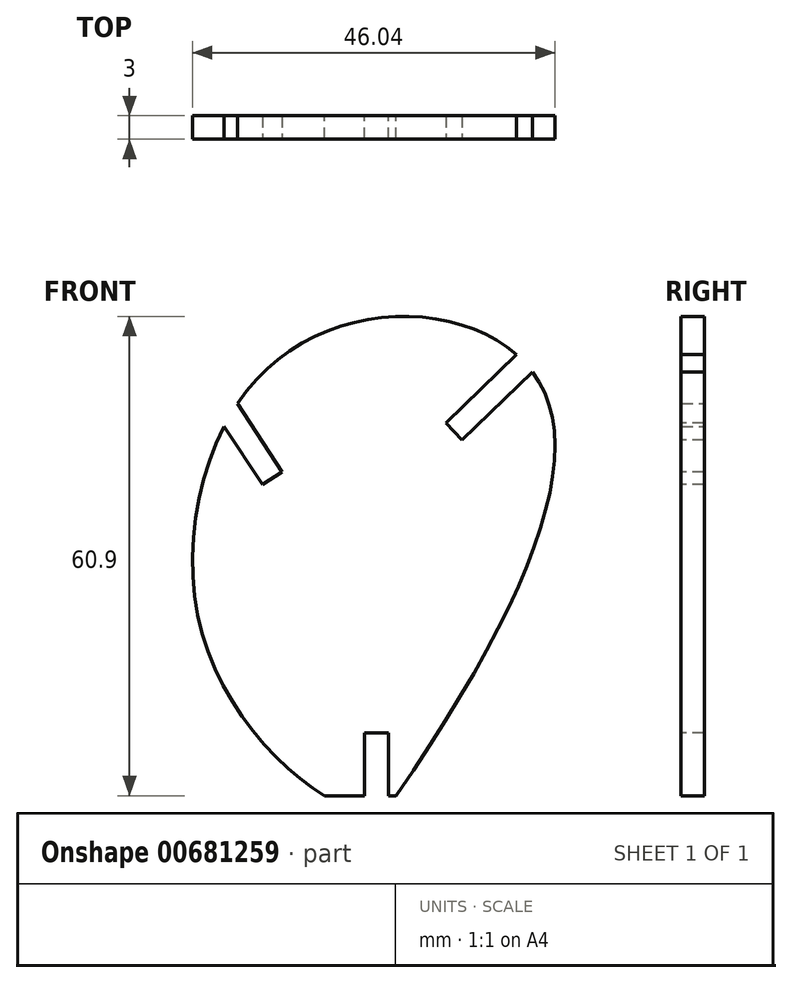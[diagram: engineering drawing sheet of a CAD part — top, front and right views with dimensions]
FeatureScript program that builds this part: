
annotation { "Feature Type Name" : "Feature", "Feature Type Description" : "" }
export const myFeature = defineFeature(function(context is Context, id is Id, definition is map)
    precondition{}
    {
        {
            assignVariable(context, id + "F0", {"name" : "MaterialDepth", "anyValue" : 3 * mm});
        }
        {
            var Q0;
            Q0=qCreatedBy(makeId("Front.planeOp"),FACE);
            var sketch = newSketch(context, id + "F1", { "sketchPlane" : qUnion([Q0])});
            skLineSegment(sketch, "E0", {"start": v(0, 53.6) * mm, "end": v(0, -7.3) * mm, "construction": true});
            skFitSpline(sketch, "E1", {"points": [v(-6.58, 0) * mm, v(-22.5, 22) * mm, v(-15.2, 52.94) * mm, v(6.9, 60.67) * mm, v(21.7, 50.29) * mm, v(2.48, 0) * mm], "startDerivative": vector(-102.35, 61.83) * mm, "endDerivative": vector(-172.56, -250.25) * mm});
            skLineSegment(sketch, "E2", {"start": v(-6.58, 0) * mm, "end": v(2.48, 0) * mm});
            skSolve(sketch);
        }
        {
            var Q0;
            Q0=makeQuery(id+"F1.imprint","IMPRINT",FACE,{"disambiguationData":[TD([[makeQuery(id+"F1.imprint","IMPRINT",EDGE,{"derivedFrom":sQuery(id+"F1.wireOp",EDGE,"E1")}),-1.0]])]});
            extrude(context, id + "F2", {"entities" : qUnion([Q0]), "endBound" : BoundingType.SYMMETRIC, "depth" : getVariable(context, 'MaterialDepth'), "offsetDistance" : 25 * mm});
        }
        {
            var Q0;
            Q0=makeQuery(id+"F2.opExtrude","CAP_FACE",FACE,{"disambiguationData":[OSD([sQuery(id+"F1.wireOp",EDGE,"E1"),sQuery(id+"F1.wireOp",EDGE,"E2")])],"isStart":false});
            var sketch = newSketch(context, id + "F3", { "sketchPlane" : qUnion([Q0])});
            skPoint(sketch, "E3", {"position": v(-18.52, 48.4) * mm});
            skLineSegment(sketch, "E4", {"start": v(-18.52, 48.4) * mm, "end": v(-14.84, 42.77) * mm, "construction": true});
            skLineSegment(sketch, "E5", {"start": v(-23.38, 45.24) * mm, "end": v(-18.52, 48.4) * mm, "construction": true});
            skLineSegment(sketch, "E6", {"start": v(-25.05, 55.66) * mm, "end": v(-23.8, 56.48) * mm});
            skLineSegment(sketch, "E7.MirrorCS", {"start": v(-14.51, 39.52) * mm, "end": v(-13.26, 40.34) * mm});
            skLineSegment(sketch, "E8", {"start": v(-25.05, 55.66) * mm, "end": v(-14.51, 39.52) * mm});
            skLineSegment(sketch, "E9.MirrorCS", {"start": v(-22.54, 57.3) * mm, "end": v(-23.8, 56.48) * mm});
            skLineSegment(sketch, "E10.MirrorCS", {"start": v(-22.54, 57.3) * mm, "end": v(-12, 41.16) * mm});
            skLineSegment(sketch, "E11.MirrorCS", {"start": v(-12, 41.16) * mm, "end": v(-13.26, 40.34) * mm});
            skPoint(sketch, "E12", {"position": v(18.83, 55) * mm});
            skLineSegment(sketch, "E13", {"start": v(18.83, 55) * mm, "end": v(12.2, 48.6) * mm, "construction": true});
            skLineSegment(sketch, "E14", {"start": v(18.83, 55) * mm, "end": v(19.82, 53.97) * mm, "construction": true});
            skLineSegment(sketch, "E15", {"start": v(10.88, 45.22) * mm, "end": v(9.84, 46.3) * mm});
            skLineSegment(sketch, "E16.MirrorCS", {"start": v(28.86, 62.6) * mm, "end": v(27.81, 63.68) * mm});
            skLineSegment(sketch, "E17", {"start": v(10.88, 45.22) * mm, "end": v(28.86, 62.6) * mm});
            skLineSegment(sketch, "E18.MirrorCS", {"start": v(8.8, 47.38) * mm, "end": v(9.84, 46.3) * mm});
            skLineSegment(sketch, "E19.MirrorCS", {"start": v(8.8, 47.38) * mm, "end": v(26.77, 64.76) * mm});
            skLineSegment(sketch, "E20.MirrorCS", {"start": v(26.77, 64.76) * mm, "end": v(27.81, 63.68) * mm});
            skLineSegment(sketch, "E21.bottom", {"start": v(1.5, -8) * mm, "end": v(-1.5, -8) * mm});
            skLineSegment(sketch, "E21.top", {"start": v(1.5, 8) * mm, "end": v(-1.5, 8) * mm});
            skLineSegment(sketch, "E21.left", {"start": v(1.5, -8) * mm, "end": v(1.5, 8) * mm});
            skLineSegment(sketch, "E21.right", {"start": v(-1.5, -8) * mm, "end": v(-1.5, 8) * mm});
            skPoint(sketch, "E21.middle", {"position": v(0, 0) * mm});
            skSolve(sketch);
        }
        {
            var Q0;
            Q0=qSketchRegion(id+"F3",true);
            extrude(context, id + "F4", {"entities" : qUnion([Q0]), "operationType" : NewBodyOperationType.REMOVE, "oppositeDirection" : true, "depth" : 25 * mm, "offsetDistance" : 25 * mm});
        }
    });
